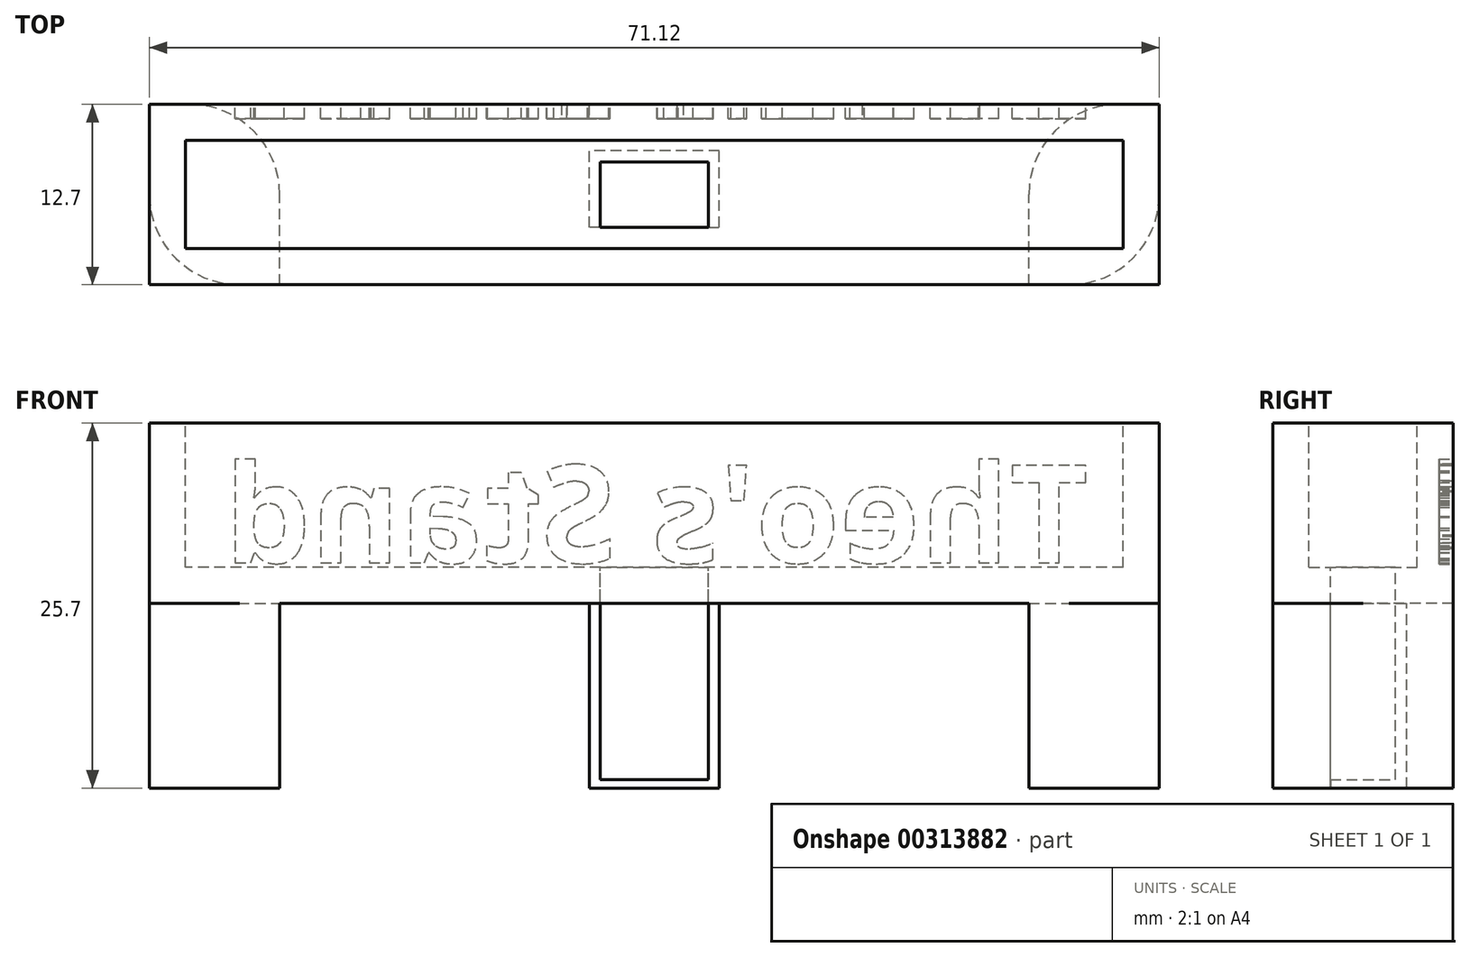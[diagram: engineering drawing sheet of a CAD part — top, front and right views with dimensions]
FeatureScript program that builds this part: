
annotation { "Feature Type Name" : "Feature", "Feature Type Description" : "" }
export const myFeature = defineFeature(function(context is Context, id is Id, definition is map)
    precondition{}
    {
        {
            var Q0;
            Q0=qCreatedBy(makeId("Top.planeOp"),FACE);
            var sketch = newSketch(context, id + "F0", { "sketchPlane" : qUnion([Q0])});
            skLineSegment(sketch, "E0.bottom", {"start": v(35.56, -6.35) * mm, "end": v(-35.56, -6.35) * mm});
            skLineSegment(sketch, "E0.top", {"start": v(35.56, 6.35) * mm, "end": v(-35.56, 6.35) * mm});
            skLineSegment(sketch, "E0.left", {"start": v(35.56, -6.35) * mm, "end": v(35.56, 6.35) * mm});
            skLineSegment(sketch, "E0.right", {"start": v(-35.56, -6.35) * mm, "end": v(-35.56, 6.35) * mm});
            skPoint(sketch, "E0.middle", {"position": v(0, 0) * mm});
            skSolve(sketch);
        }
        {
            var Q0;
            Q0=makeQuery(id+"F0.imprint","IMPRINT",FACE,{"disambiguationData":[TD([[makeQuery(id+"F0.imprint","IMPRINT",EDGE,{"derivedFrom":sQuery(id+"F0.wireOp",EDGE,"E0.bottom")}),-1.0]])]});
            extrude(context, id + "F1", {"entities" : qUnion([Q0]), "oppositeDirection" : true, "depth" : 12.7 * mm});
        }
        {
            var Q0;
            Q0=makeQuery(id+"F1.opExtrude","CAP_FACE",FACE,{"disambiguationData":[OSD([sQuery(id+"F0.wireOp",EDGE,"E0.bottom"),sQuery(id+"F0.wireOp",EDGE,"E0.top"),sQuery(id+"F0.wireOp",EDGE,"E0.left"),sQuery(id+"F0.wireOp",EDGE,"E0.right")])],"isStart":true});
            shell(context, id + "F2", {"entities" : qUnion([Q0]), "thickness" : 2.54 * mm});
        }
        {
            var Q0;
            Q0=makeQuery(id+"F2.opShell","OFFSET_FACE",FACE,{"disambiguationData":[OSD([sQuery(id+"F0.wireOp",EDGE,"E0.bottom"),sQuery(id+"F0.wireOp",EDGE,"E0.top"),sQuery(id+"F0.wireOp",EDGE,"E0.left"),sQuery(id+"F0.wireOp",EDGE,"E0.right")])]});
            var sketch = newSketch(context, id + "F3", { "sketchPlane" : qUnion([Q0])});
            skLineSegment(sketch, "E1.bottom", {"start": v(-3.8, 2.3) * mm, "end": v(3.8, 2.3) * mm});
            skLineSegment(sketch, "E1.top", {"start": v(-3.8, -2.3) * mm, "end": v(3.8, -2.3) * mm});
            skLineSegment(sketch, "E1.left", {"start": v(-3.8, 2.3) * mm, "end": v(-3.8, -2.3) * mm});
            skLineSegment(sketch, "E1.right", {"start": v(3.8, 2.3) * mm, "end": v(3.8, -2.3) * mm});
            skPoint(sketch, "E1.middle", {"position": v(0, 0) * mm});
            skSolve(sketch);
        }
        {
            var Q0;
            Q0 = qSketchRegion(id + "F3", true);
            extrude(context, id + "F4", {"entities" : qUnion([Q0]), "operationType" : NewBodyOperationType.REMOVE, "oppositeDirection" : true, "depth" : 25.4 * mm});
        }
        {
            var Q0;
            Q0=makeQuery(id+"F1.opExtrude","CAP_FACE",FACE,{"disambiguationData":[OSD([sQuery(id+"F0.wireOp",EDGE,"E0.bottom"),sQuery(id+"F0.wireOp",EDGE,"E0.top"),sQuery(id+"F0.wireOp",EDGE,"E0.left"),sQuery(id+"F0.wireOp",EDGE,"E0.right")])],"isStart":false});
            var sketch = newSketch(context, id + "F5", { "sketchPlane" : qUnion([Q0])});
            skLineSegment(sketch, "E2.bottom", {"start": v(-3.8, -2.3) * mm, "end": v(3.8, -2.3) * mm});
            skLineSegment(sketch, "E2.top", {"start": v(-3.8, -3.08) * mm, "end": v(3.8, -3.08) * mm});
            skLineSegment(sketch, "E2.left", {"start": v(-3.8, -2.3) * mm, "end": v(-3.8, -3.08) * mm});
            skLineSegment(sketch, "E2.right", {"start": v(3.8, -2.3) * mm, "end": v(3.8, -3.08) * mm});
            skLineSegment(sketch, "E3.bottom", {"start": v(3.8, 2.3) * mm, "end": v(4.58, 2.3) * mm});
            skLineSegment(sketch, "E3.top", {"start": v(3.8, -3.08) * mm, "end": v(4.58, -3.08) * mm});
            skLineSegment(sketch, "E3.left", {"start": v(3.8, 2.3) * mm, "end": v(3.8, -3.08) * mm});
            skLineSegment(sketch, "E3.right", {"start": v(4.58, 2.3) * mm, "end": v(4.58, -3.08) * mm});
            skLineSegment(sketch, "E4.bottom", {"start": v(-3.8, 2.3) * mm, "end": v(-4.58, 2.3) * mm});
            skLineSegment(sketch, "E4.top", {"start": v(-3.8, -3.08) * mm, "end": v(-4.58, -3.08) * mm});
            skLineSegment(sketch, "E4.left", {"start": v(-3.8, 2.3) * mm, "end": v(-3.8, -3.08) * mm});
            skLineSegment(sketch, "E4.right", {"start": v(-4.58, 2.3) * mm, "end": v(-4.58, -3.08) * mm});
            skPoint(sketch, "E5.visualSharp", {"position": v(-35.56, 6.35) * mm});
            skLineSegment(sketch, "E6.bottom", {"start": v(-29.2, 6.35) * mm, "end": v(-26.38, 6.35) * mm});
            skLineSegment(sketch, "E6.top", {"start": v(-35.56, -6.35) * mm, "end": v(-32.73, -6.35) * mm});
            skLineSegment(sketch, "E6.left", {"start": v(-35.56, 0) * mm, "end": v(-35.56, -6.35) * mm});
            skLineSegment(sketch, "E6.right", {"start": v(-26.38, 6.35) * mm, "end": v(-26.38, 0) * mm});
            skPoint(sketch, "E7.visualSharp", {"position": v(-26.38, -6.35) * mm});
            skArc(sketch, "E7.filletArc", {"start": v(-32.73, -6.35) * mm, "mid": v(-28.24, -4.5) * mm, "end": v(-26.38, 0) * mm});
            skArc(sketch, "E8.filletArc", {"start": v(-29.2, 6.35) * mm, "mid": v(-33.7, 4.5) * mm, "end": v(-35.56, 0) * mm});
            skPoint(sketch, "E9.MirrorP", {"position": v(35.56, 6.35) * mm});
            skArc(sketch, "E10.MirrorCS", {"start": v(32.73, -6.35) * mm, "mid": v(28.24, -4.5) * mm, "end": v(26.38, 0) * mm});
            skPoint(sketch, "E11.MirrorP", {"position": v(26.38, -6.35) * mm});
            skLineSegment(sketch, "E12.MirrorCS", {"start": v(26.38, 6.35) * mm, "end": v(26.38, 0) * mm});
            skArc(sketch, "E13.MirrorCS", {"start": v(29.2, 6.35) * mm, "mid": v(33.7, 4.5) * mm, "end": v(35.56, 0) * mm});
            skLineSegment(sketch, "E14.MirrorCS", {"start": v(29.2, 6.35) * mm, "end": v(26.38, 6.35) * mm});
            skLineSegment(sketch, "E15.MirrorCS", {"start": v(35.56, -6.35) * mm, "end": v(32.73, -6.35) * mm});
            skLineSegment(sketch, "E16.MirrorCS", {"start": v(35.56, 0) * mm, "end": v(35.56, -6.35) * mm});
            skSolve(sketch);
        }
        {
            var Q0;
            Q0 = qSketchRegion(id + "F5", true);
            extrude(context, id + "F6", {"entities" : qUnion([Q0]), "operationType" : NewBodyOperationType.ADD, "depth" : 13 * mm});
        }
        {
            var Q0;
            Q0=makeQuery(id+"F6.boolean.opBoolean","MERGE",FACE,{"derivedFrom":[makeQuery(id+"F4.boolean.opBoolean","COPY",FACE,{"derivedFrom":makeQuery(id+"F4.opExtrude","SWEPT_FACE",FACE,{"disambiguationData":[OSD([sQuery(id+"F3.wireOp",EDGE,"E1.bottom")])]})}),makeQuery(id+"F6.opExtrude","SWEPT_FACE",FACE,{"disambiguationData":[OSD([sQuery(id+"F5.wireOp",EDGE,"E2.bottom")])]})]});
            var sketch = newSketch(context, id + "F7", { "sketchPlane" : qUnion([Q0])});
            skLineSegment(sketch, "E17.bottom", {"start": v(3.8, -25.7) * mm, "end": v(-3.8, -25.7) * mm});
            skLineSegment(sketch, "E17.top", {"start": v(3.8, -25.11) * mm, "end": v(-3.8, -25.11) * mm});
            skLineSegment(sketch, "E17.left", {"start": v(3.8, -25.7) * mm, "end": v(3.8, -25.11) * mm});
            skLineSegment(sketch, "E17.right", {"start": v(-3.8, -25.7) * mm, "end": v(-3.8, -25.11) * mm});
            skSolve(sketch);
        }
        {
            var Q0;
            Q0=makeQuery(id+"F7.imprint","IMPRINT",FACE,{"disambiguationData":[TD([[makeQuery(id+"F7.imprint","IMPRINT",EDGE,{"derivedFrom":sQuery(id+"F7.wireOp",EDGE,"E17.bottom")}),1.0]])]});
            extrude(context, id + "F8", {"entities" : qUnion([Q0]), "operationType" : NewBodyOperationType.ADD, "depth" : 4.6 * mm});
        }
        {
            var Q0;
            Q0=makeQuery(id+"F6.boolean.opBoolean","MERGE",FACE,{"derivedFrom":[makeQuery(id+"F1.opExtrude","SWEPT_FACE",FACE,{"disambiguationData":[OSD([sQuery(id+"F0.wireOp",EDGE,"E0.top")])]}),makeQuery(id+"F6.opExtrude","SWEPT_FACE",FACE,{"disambiguationData":[OSD([sQuery(id+"F5.wireOp",EDGE,"E6.top")])]}),makeQuery(id+"F6.opExtrude","SWEPT_FACE",FACE,{"disambiguationData":[OSD([sQuery(id+"F5.wireOp",EDGE,"E15.MirrorCS")])]})]});
            var sketch = newSketch(context, id + "F9", { "sketchPlane" : qUnion([Q0])});
            skText(sketch, "E18", { "text": "Theo\'s Stand", "fontName": "OpenSans-Bold.ttf"});
            const initialGuessF9  = {"E18": [-0.03057, -0.00982, 1, 0, 0.0069]};
            skSetInitialGuess(sketch, initialGuessF9);
            skSolve(sketch);
        }
        {
            var Q0;
            Q0 = qSketchRegion(id + "F9", true);
            var Q1;
            Q1 = qConstructionFilter(qBodyType(qCreatedBy(id + "F9" ,EDGE), BodyType.WIRE), ConstructionObject.NO);
            extrude(context, id + "F10", {"entities" : qUnion([Q0]), "operationType" : NewBodyOperationType.REMOVE, "surfaceEntities" : qUnion([Q1]), "oppositeDirection" : true, "depth" : 1 * mm});
        }
    });
